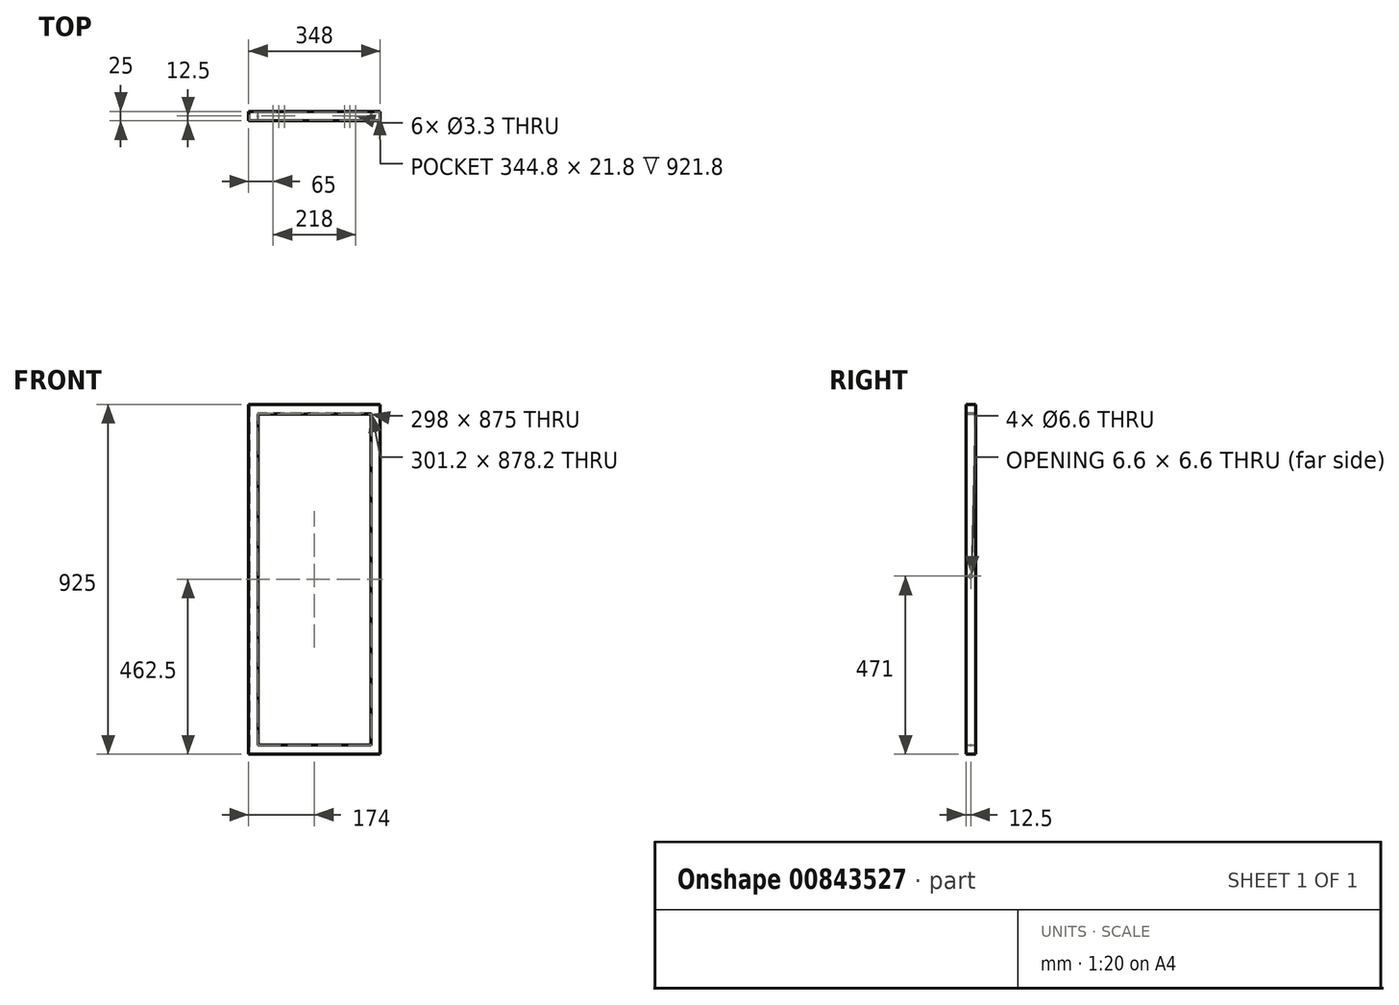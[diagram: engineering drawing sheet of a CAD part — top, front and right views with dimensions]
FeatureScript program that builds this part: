
annotation { "Feature Type Name" : "Feature", "Feature Type Description" : "" }
export const myFeature = defineFeature(function(context is Context, id is Id, definition is map)
    precondition{}
    {
        {
            var Q0;
            Q0=qCreatedBy(makeId("Front.planeOp"),FACE);
            var sketch = newSketch(context, id + "F0", { "sketchPlane" : qUnion([Q0])});
            skLineSegment(sketch, "E0.bottom", {"start": v(174, 462.5) * mm, "end": v(-174, 462.5) * mm});
            skLineSegment(sketch, "E0.top", {"start": v(174, -462.5) * mm, "end": v(-174, -462.5) * mm});
            skLineSegment(sketch, "E0.left", {"start": v(174, 462.5) * mm, "end": v(174, -462.5) * mm});
            skLineSegment(sketch, "E0.right", {"start": v(-174, 462.5) * mm, "end": v(-174, -462.5) * mm});
            skPoint(sketch, "E0.middle", {"position": v(0, 0) * mm});
            skLineSegment(sketch, "E1.bottom", {"start": v(149, 437.5) * mm, "end": v(-149, 437.5) * mm});
            skLineSegment(sketch, "E1.top", {"start": v(149, -437.5) * mm, "end": v(-149, -437.5) * mm});
            skLineSegment(sketch, "E1.left", {"start": v(149, 437.5) * mm, "end": v(149, -437.5) * mm});
            skLineSegment(sketch, "E1.right", {"start": v(-149, 437.5) * mm, "end": v(-149, -437.5) * mm});
            skSolve(sketch);
        }
        {
            var Q0;
            Q0=makeQuery(id+"F0.imprint","IMPRINT",FACE,{"disambiguationData":[TD([[makeQuery(id+"F0.imprint","IMPRINT",EDGE,{"derivedFrom":sQuery(id+"F0.wireOp",EDGE,"E0.bottom")}),1.0]])]});
            extrude(context, id + "F1", {"entities" : qUnion([Q0]), "depth" : 25 * mm, "offsetDistance" : 25 * mm});
        }
        {
            var Q0;
            Q0=makeQuery(id+"F1.opExtrude","SWEPT_FACE",FACE,{"disambiguationData":[OSD([sQuery(id+"F0.wireOp",EDGE,"E0.left")])]});
            var sketch = newSketch(context, id + "F2", { "sketchPlane" : qUnion([Q0])});
            skPoint(sketch, "E2", {"position": v(-12.5, 8.5) * mm});
            skSolve(sketch);
        }
        {
            var Q0;
            Q0=sQuery(id+"F2.wireOp",VERTEX,"E2");
            var Q1;
            Q1=makeQuery(id+"F1.opExtrude","SWEPT_BODY",BODY,{"disambiguationData":[OSD([sQuery(id+"F0.wireOp",EDGE,"E0.bottom"),sQuery(id+"F0.wireOp",EDGE,"E0.top"),sQuery(id+"F0.wireOp",EDGE,"E0.left"),sQuery(id+"F0.wireOp",EDGE,"E0.right"),sQuery(id+"F0.wireOp",EDGE,"E1.bottom"),sQuery(id+"F0.wireOp",EDGE,"E1.top"),sQuery(id+"F0.wireOp",EDGE,"E1.left"),sQuery(id+"F0.wireOp",EDGE,"E1.right")])]});
            hole(context, id + "F3", {"style" : HoleStyle.SIMPLE, "endStyle" : HoleEndStyle.BLIND, "standardTappedOrClearance" : lookupTablePath({ "fit" : "Normal", "standard" : "ISO", "size" : "M6", "type" : "Clearance" }), "standardBlindInLast" : lookupTablePath({ "fit" : "Normal", "standard" : "ISO", "size" : "M6", "type" : "Clearance" }), "holeDiameter" : 6.6 * mm, "majorDiameter" : 5 * mm, "holeDepth" : 500 * mm, "isTappedThrough" : true, "tappedDepth" : 12 * mm, "tapClearance" : 3, "locations" : qUnion([Q0]), "scope" : qUnion([Q1])});
        }
        {
            var Q0;
            Q0=makeQuery(id+"F1.opExtrude","SWEPT_FACE",FACE,{"disambiguationData":[OSD([sQuery(id+"F0.wireOp",EDGE,"E1.top")])]});
            var sketch = newSketch(context, id + "F4", { "sketchPlane" : qUnion([Q0])});
            skLineSegment(sketch, "E3", {"start": v(-149, -12.5) * mm, "end": v(149, -12.5) * mm, "construction": true});
            skCircle(sketch, "E4", {"center": v(109, -12.5) * mm, "radius": 1.65 * mm});
            skCircle(sketch, "E5", {"center": v(94, -12.5) * mm, "radius": 1.65 * mm});
            skCircle(sketch, "E6", {"center": v(79, -12.5) * mm, "radius": 1.65 * mm});
            skCircle(sketch, "E7", {"center": v(-79, -12.5) * mm, "radius": 1.65 * mm});
            skCircle(sketch, "E8", {"center": v(-94, -12.5) * mm, "radius": 1.65 * mm});
            skCircle(sketch, "E9", {"center": v(-109, -12.5) * mm, "radius": 1.65 * mm});
            skSolve(sketch);
        }
        {
            var Q0;
            Q0 = qSketchRegion(id + "F4", true);
            extrude(context, id + "F5", {"entities" : qUnion([Q0]), "operationType" : NewBodyOperationType.REMOVE, "oppositeDirection" : true, "depth" : 4 * mm, "offsetDistance" : 25 * mm});
        }
        {
            var Q0;
            Q0=makeQuery(id+"F1.opExtrude","CAP_FACE",FACE,{"disambiguationData":[OSD([sQuery(id+"F0.wireOp",EDGE,"E0.bottom"),sQuery(id+"F0.wireOp",EDGE,"E0.top"),sQuery(id+"F0.wireOp",EDGE,"E0.left"),sQuery(id+"F0.wireOp",EDGE,"E0.right"),sQuery(id+"F0.wireOp",EDGE,"E1.bottom"),sQuery(id+"F0.wireOp",EDGE,"E1.top"),sQuery(id+"F0.wireOp",EDGE,"E1.left"),sQuery(id+"F0.wireOp",EDGE,"E1.right")])],"isStart":false});
            cPlane(context, id + "F6", {"entities" : qUnion([Q0]), "cplaneType" : CPlaneType.OFFSET, "offset" : 1.6 * mm, "oppositeDirection" : true, "width" : 150 * mm, "height" : 150 * mm});
        }
        {
            var Q0;
            Q0=qCreatedBy(id+"F6.planeOp",FACE);
            var sketch = newSketch(context, id + "F7", { "sketchPlane" : qUnion([Q0])});
            skLineSegment(sketch, "E10.bottom", {"start": v(172.4, 460.9) * mm, "end": v(-172.4, 460.9) * mm});
            skLineSegment(sketch, "E10.top", {"start": v(172.4, -460.9) * mm, "end": v(-172.4, -460.9) * mm});
            skLineSegment(sketch, "E10.left", {"start": v(172.4, 460.9) * mm, "end": v(172.4, -460.9) * mm});
            skLineSegment(sketch, "E10.right", {"start": v(-172.4, 460.9) * mm, "end": v(-172.4, -460.9) * mm});
            skPoint(sketch, "E10.middle", {"position": v(0, 0) * mm});
            skLineSegment(sketch, "E11.bottom", {"start": v(150.6, 439.1) * mm, "end": v(-150.6, 439.1) * mm});
            skLineSegment(sketch, "E11.top", {"start": v(150.6, -439.1) * mm, "end": v(-150.6, -439.1) * mm});
            skLineSegment(sketch, "E11.left", {"start": v(150.6, 439.1) * mm, "end": v(150.6, -439.1) * mm});
            skLineSegment(sketch, "E11.right", {"start": v(-150.6, 439.1) * mm, "end": v(-150.6, -439.1) * mm});
            skSolve(sketch);
        }
        {
            var Q0;
            Q0 = qSketchRegion(id + "F7", true);
            extrude(context, id + "F8", {"entities" : qUnion([Q0]), "operationType" : NewBodyOperationType.REMOVE, "oppositeDirection" : true, "depth" : (25 - 3.2) * mm, "offsetDistance" : 25 * mm});
        }
    });
